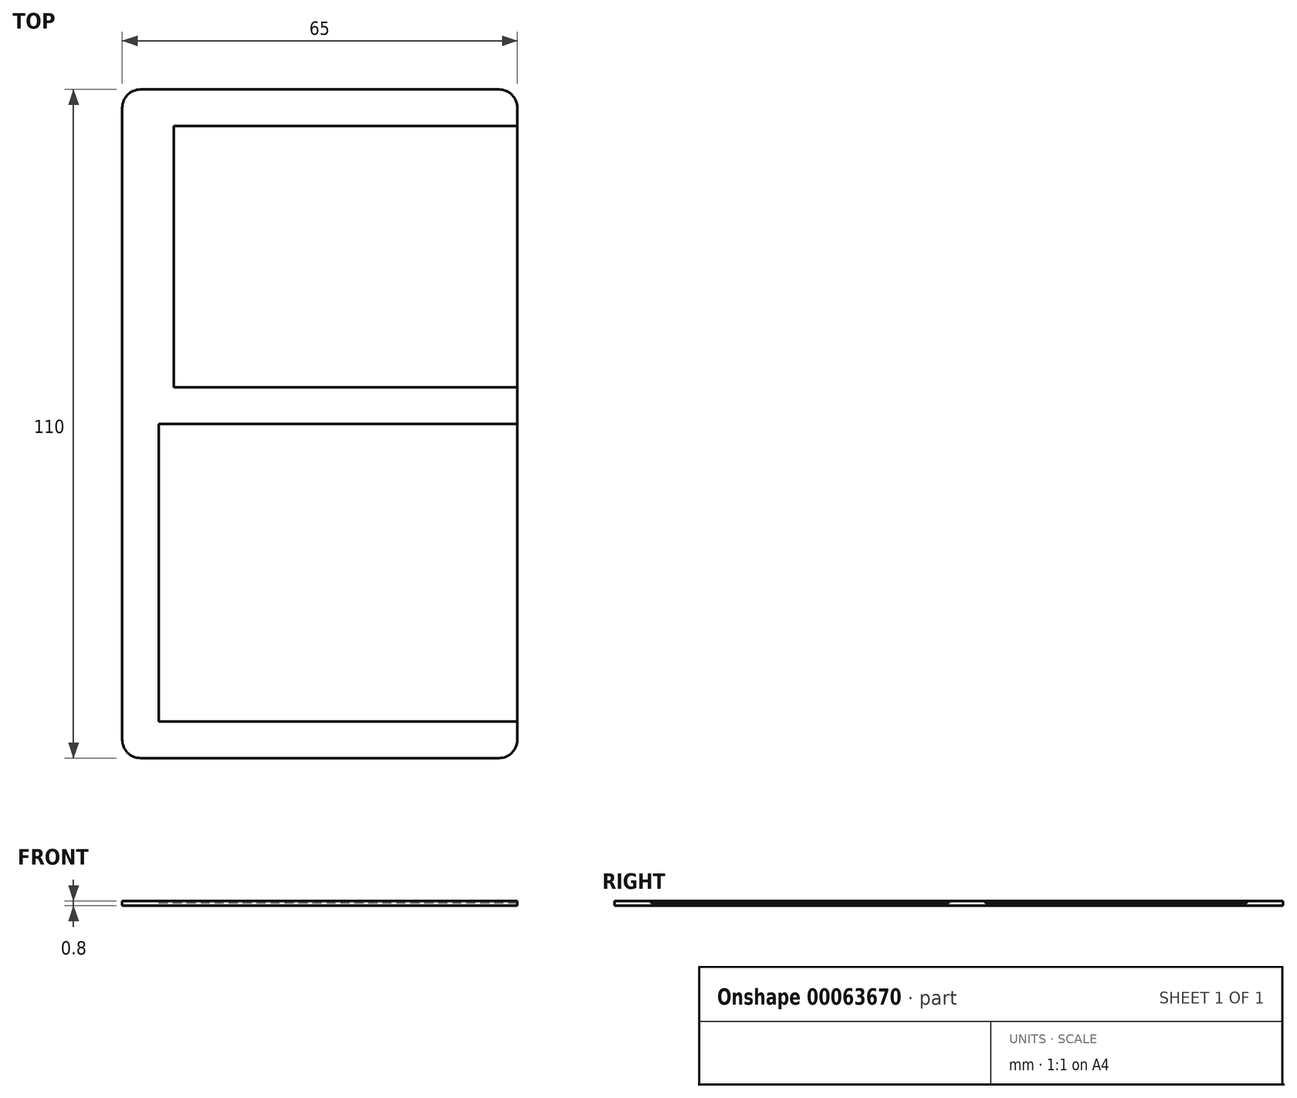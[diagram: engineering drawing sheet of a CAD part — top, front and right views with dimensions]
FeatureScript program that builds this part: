
annotation { "Feature Type Name" : "Feature", "Feature Type Description" : "" }
export const myFeature = defineFeature(function(context is Context, id is Id, definition is map)
    precondition{}
    {
        {
            assignVariable(context, id + "F0", {"name" : "gap", "anyValue" : 6});
        }
        {
            var Q0;
            Q0=qCreatedBy(makeId("Top.planeOp"),FACE);
            var sketch = newSketch(context, id + "F1", { "sketchPlane" : qUnion([Q0])});
            skLineSegment(sketch, "E0.rect.bottom", {"start": v(26.5, -24.5) * mm, "end": v(-26.5, -24.5) * mm});
            skLineSegment(sketch, "E0.rect.top", {"start": v(26.5, 24.5) * mm, "end": v(-26.5, 24.5) * mm});
            skLineSegment(sketch, "E0.rect.left", {"start": v(26.5, -24.5) * mm, "end": v(26.5, 24.5) * mm});
            skLineSegment(sketch, "E0.rect.right", {"start": v(-26.5, -24.5) * mm, "end": v(-26.5, 24.5) * mm});
            skPoint(sketch, "E0.rect.middle", {"position": v(0, 0) * mm});
            skLineSegment(sketch, "E1.rect.bottom", {"start": v(24, 30.5) * mm, "end": v(-24, 30.5) * mm});
            skLineSegment(sketch, "E1.rect.top", {"start": v(24, 73.5) * mm, "end": v(-24, 73.5) * mm});
            skLineSegment(sketch, "E1.rect.left", {"start": v(24, 30.5) * mm, "end": v(24, 73.5) * mm});
            skLineSegment(sketch, "E1.rect.right", {"start": v(-24, 30.5) * mm, "end": v(-24, 73.5) * mm});
            skPoint(sketch, "E1.rect.middle", {"position": v(0, 52) * mm});
            skPoint(sketch, "E1.rect.middle.positionSnap0", {"position": v(0, 24.5) * mm});
            skPoint(sketch, "E1.rect.centerSnap0", {"position": v(0, 24.5) * mm});
            skLineSegment(sketch, "E2", {"start": v(-32.5, -30.5) * mm, "end": v(-32.5, 79.5) * mm});
            skLineSegment(sketch, "E3", {"start": v(-32.5, 79.5) * mm, "end": v(32.5, 79.5) * mm});
            skLineSegment(sketch, "E4", {"start": v(32.5, 79.5) * mm, "end": v(32.5, -30.5) * mm});
            skLineSegment(sketch, "E5", {"start": v(32.5, -30.5) * mm, "end": v(-32.5, -30.5) * mm});
            skLineSegment(sketch, "E6", {"start": v(0, 52) * mm, "end": v(0, 0) * mm, "construction": true});
            skSolve(sketch);
        }
        {
            var Q0;
            Q0=makeQuery(id+"F1.imprint","IMPRINT",FACE,{"disambiguationData":[TD([[makeQuery(id+"F1.imprint","IMPRINT",EDGE,{"derivedFrom":sQuery(id+"F1.wireOp",EDGE,"E0.rect.bottom")}),1.0]])]});
            var Q1;
            Q1=makeQuery(id+"F1.imprint","IMPRINT",FACE,{"disambiguationData":[TD([[makeQuery(id+"F1.imprint","IMPRINT",EDGE,{"derivedFrom":sQuery(id+"F1.wireOp",EDGE,"E1.rect.bottom")}),-1.0]])]});
            var Q2;
            Q2=makeQuery(id+"F1.imprint","IMPRINT",FACE,{"disambiguationData":[TD([[makeQuery(id+"F1.imprint","IMPRINT",EDGE,{"derivedFrom":sQuery(id+"F1.wireOp",EDGE,"E0.rect.bottom")}),-1.0]])]});
            extrude(context, id + "F2", {"entities" : qUnion([Q0, Q1, Q2]), "oppositeDirection" : true, "depth" : 0.4 * mm});
        }
        {
            var Q0;
            Q0=makeQuery(id+"F1.imprint","IMPRINT",FACE,{"disambiguationData":[TD([[makeQuery(id+"F1.imprint","IMPRINT",EDGE,{"derivedFrom":sQuery(id+"F1.wireOp",EDGE,"E0.rect.bottom")}),1.0]])]});
            extrude(context, id + "F3", {"entities" : qUnion([Q0]), "operationType" : NewBodyOperationType.ADD, "depth" : 0.4 * mm});
        }
        {
            var Q0;
            Q0=makeQuery(id+"F3.opExtrude","SWEPT_FACE",FACE,{"disambiguationData":[OSD([sQuery(id+"F1.wireOp",EDGE,"E0.rect.left")])]});
            var Q1;
            Q1=makeQuery(id+"F3.opExtrude","SWEPT_FACE",FACE,{"disambiguationData":[OSD([sQuery(id+"F1.wireOp",EDGE,"E1.rect.left")])]});
            var Q2;
            {var subQ0=sQuery(id+"F1.wireOp",EDGE,"E4");Q2=makeQuery(id+"F3.boolean.opBoolean","MERGE",FACE,{"derivedFrom":[makeQuery(id+"F2.opExtrude","SWEPT_FACE",FACE,{"disambiguationData":[OSD([subQ0])]}),makeQuery(id+"F3.opExtrude","SWEPT_FACE",FACE,{"disambiguationData":[OSD([subQ0])]})]});}
            extrude(context, id + "F4", {"entities" : qUnion([Q0, Q1]), "operationType" : NewBodyOperationType.REMOVE, "endBound" : BoundingType.UP_TO_SURFACE, "oppositeDirection" : true, "endBoundEntityFace" : qUnion([Q2]), "depth" : 25 * mm});
        }
        {
            var Q0;
            {var subQ0=sQuery(id+"F1.wireOp",EDGE,"E3");var subQ1=sQuery(id+"F1.wireOp",EDGE,"E2");Q0=makeQuery(id+"F3.boolean.opBoolean","MERGE",EDGE,{"derivedFrom":[makeQuery(id+"F2.opExtrude","SWEPT_EDGE",EDGE,{"disambiguationData":[OSD([subQ1,subQ0])]}),makeQuery(id+"F3.opExtrude","SWEPT_EDGE",EDGE,{"disambiguationData":[OSD([subQ1,subQ0])]})]});}
            var Q1;
            {var subQ0=sQuery(id+"F1.wireOp",EDGE,"E4");var subQ1=sQuery(id+"F1.wireOp",EDGE,"E3");Q1=makeQuery(id+"F3.boolean.opBoolean","MERGE",EDGE,{"derivedFrom":[makeQuery(id+"F2.opExtrude","SWEPT_EDGE",EDGE,{"disambiguationData":[OSD([subQ1,subQ0])]}),makeQuery(id+"F3.opExtrude","SWEPT_EDGE",EDGE,{"disambiguationData":[OSD([subQ1,subQ0])]})]});}
            var Q2;
            {var subQ0=sQuery(id+"F1.wireOp",EDGE,"E5");var subQ1=sQuery(id+"F1.wireOp",EDGE,"E4");Q2=makeQuery(id+"F3.boolean.opBoolean","MERGE",EDGE,{"derivedFrom":[makeQuery(id+"F2.opExtrude","SWEPT_EDGE",EDGE,{"disambiguationData":[OSD([subQ1,subQ0])]}),makeQuery(id+"F3.opExtrude","SWEPT_EDGE",EDGE,{"disambiguationData":[OSD([subQ1,subQ0])]})]});}
            var Q3;
            {var subQ0=sQuery(id+"F1.wireOp",EDGE,"E5");var subQ1=sQuery(id+"F1.wireOp",EDGE,"E2");Q3=makeQuery(id+"F3.boolean.opBoolean","MERGE",EDGE,{"derivedFrom":[makeQuery(id+"F2.opExtrude","SWEPT_EDGE",EDGE,{"disambiguationData":[OSD([subQ1,subQ0])]}),makeQuery(id+"F3.opExtrude","SWEPT_EDGE",EDGE,{"disambiguationData":[OSD([subQ1,subQ0])]})]});}
            fillet(context, id + "F5", {"entities" : qUnion([Q0, Q1, Q2, Q3]), "radius" : (getVariable(context, 'gap') / 2) * mm, "tangentPropagation" : true, "allowEdgeOverflow" : false});
        }
    });
